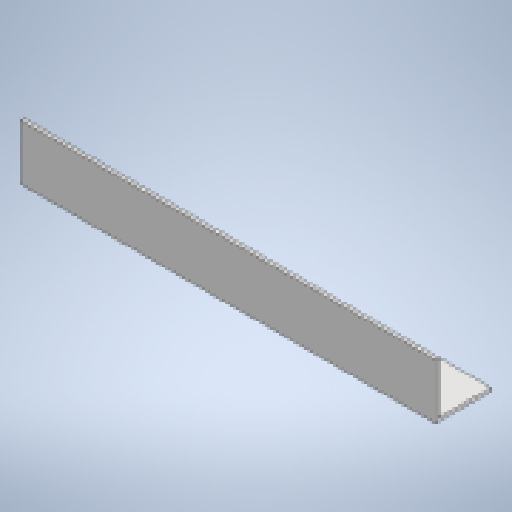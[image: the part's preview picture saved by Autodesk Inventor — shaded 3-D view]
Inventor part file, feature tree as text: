
AUTODESK INVENTOR PART (.ipt)
format: ipt  version: 2023 (Build 270158000, 158)  size: 133,120 bytes
history: native  units: in
note: dims shown in document units (in); Inventor stores cm internally (conversion verified against a paired STEP export)
features: extrude x1, sketch x1
ambient origin geometry x8: Origin, YZ Plane, XZ Plane, XY Plane, X Axis, Y Axis, Z Axis, Center Point
bodies: Solid1 (feature_tree)
feature tree (2):
  extrude  "Extrusion1"  Depth=2.0in
  sketch  "Sketch1"  dims[d0=2.0in d1=2.0in d2=0.125in d3=10.2362in d4=0.0in]
